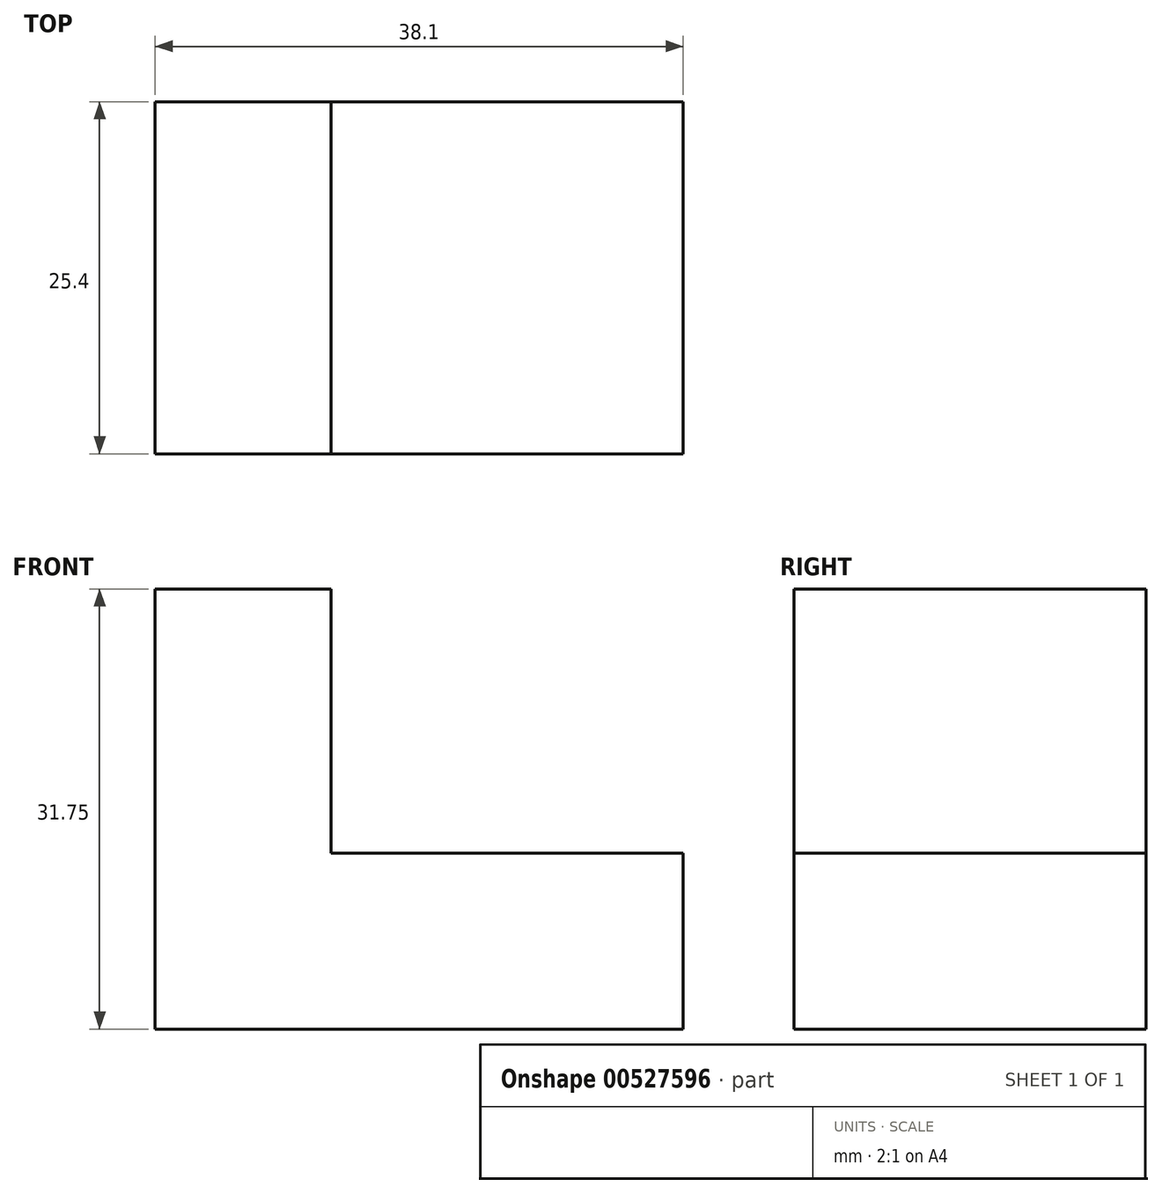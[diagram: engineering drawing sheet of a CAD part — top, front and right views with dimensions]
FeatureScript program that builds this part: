
annotation { "Feature Type Name" : "Feature", "Feature Type Description" : "" }
export const myFeature = defineFeature(function(context is Context, id is Id, definition is map)
    precondition{}
    {
        {
            var Q0;
            Q0=qCreatedBy(makeId("Front.planeOp"),FACE);
            var sketch = newSketch(context, id + "F0", { "sketchPlane" : qUnion([Q0])});
            skLineSegment(sketch, "E0", {"start": v(0, 0) * mm, "end": v(0, 31.75) * mm});
            skLineSegment(sketch, "E1", {"start": v(0, 31.75) * mm, "end": v(12.7, 31.75) * mm});
            skLineSegment(sketch, "E2", {"start": v(12.7, 31.75) * mm, "end": v(12.7, 12.7) * mm});
            skLineSegment(sketch, "E3", {"start": v(12.7, 12.7) * mm, "end": v(38.1, 12.7) * mm});
            skLineSegment(sketch, "E4", {"start": v(38.1, 12.7) * mm, "end": v(38.1, 0) * mm});
            skLineSegment(sketch, "E5", {"start": v(38.1, 0) * mm, "end": v(0, 0) * mm});
            skSolve(sketch);
        }
        {
            var Q0;
            Q0 = qSketchRegion(id + "F0", true);
            extrude(context, id + "F1", {"entities" : qUnion([Q0]), "depth" : 25.4 * mm, "offsetDistance" : 25.4 * mm});
        }
    });
